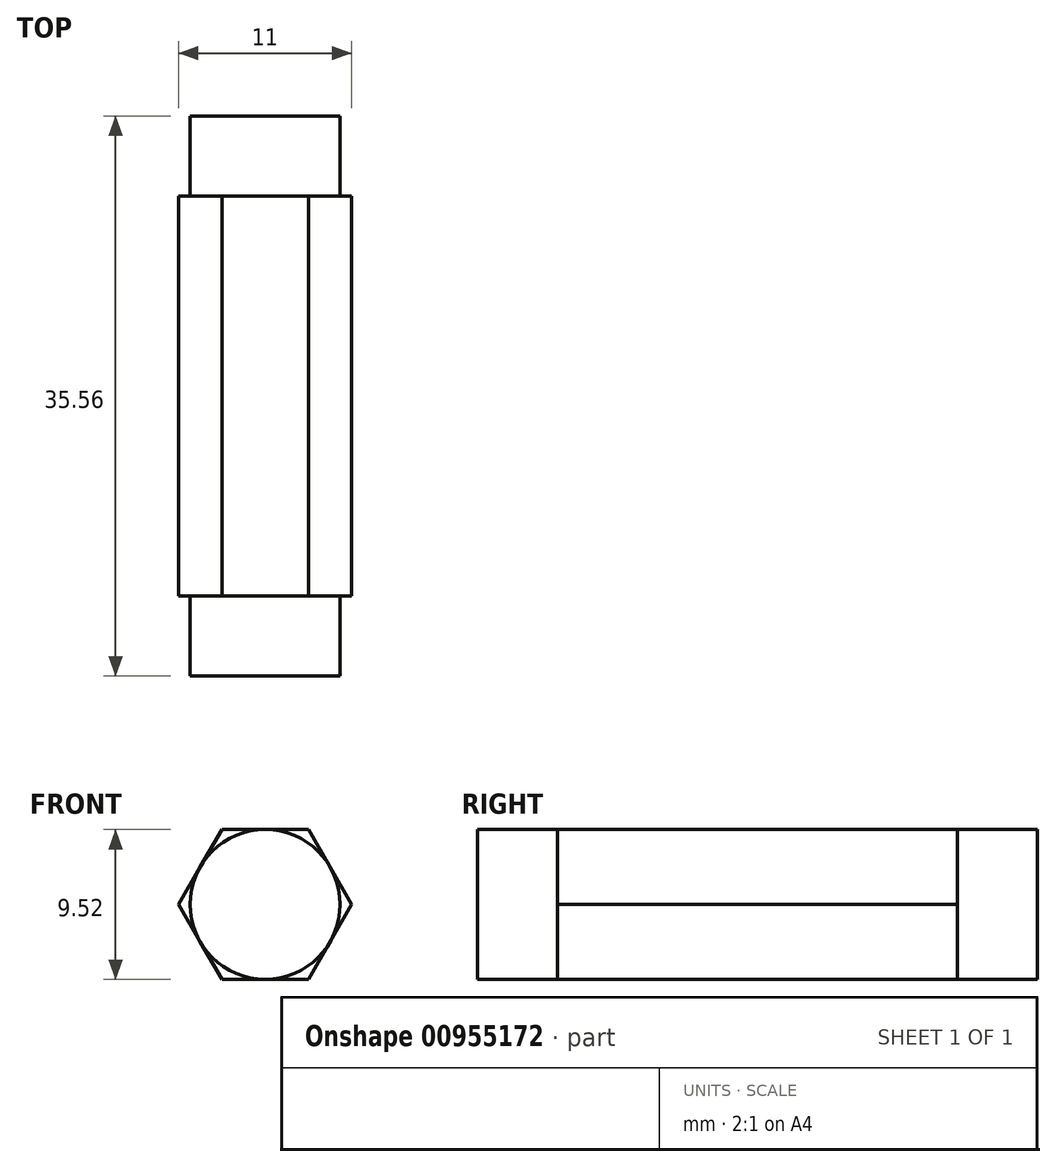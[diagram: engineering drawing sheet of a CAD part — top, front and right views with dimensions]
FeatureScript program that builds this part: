
annotation { "Feature Type Name" : "Feature", "Feature Type Description" : "" }
export const myFeature = defineFeature(function(context is Context, id is Id, definition is map)
    precondition{}
    {
        {
            var Q0;
            Q0=qCreatedBy(makeId("Front.planeOp"),FACE);
            var sketch = newSketch(context, id + "F0", { "sketchPlane" : qUnion([Q0])});
            skCircle(sketch, "E0.cCircle", {"center": v(0, 0) * mm, "radius": 4.76 * mm, "construction": true});
            skLineSegment(sketch, "E0.0", {"start": v(-2.75, 4.76) * mm, "end": v(2.75, 4.76) * mm});
            skLineSegment(sketch, "E0.1", {"start": v(2.75, 4.76) * mm, "end": v(5.5, 0) * mm});
            skLineSegment(sketch, "E0.2", {"start": v(5.5, 0) * mm, "end": v(2.75, -4.76) * mm});
            skLineSegment(sketch, "E0.3", {"start": v(2.75, -4.76) * mm, "end": v(-2.75, -4.76) * mm});
            skLineSegment(sketch, "E0.4", {"start": v(-2.75, -4.76) * mm, "end": v(-5.5, 0) * mm});
            skLineSegment(sketch, "E0.5", {"start": v(-5.5, 0) * mm, "end": v(-2.75, 4.76) * mm});
            skPoint(sketch, "E0.0.midPoint", {"position": v(0, 4.76) * mm});
            skSolve(sketch);
        }
        {
            var Q0;
            Q0=qSketchRegion(id+"F0",true);
            extrude(context, id + "F1", {"entities" : qUnion([Q0]), "depth" : 25.4 * mm, "offsetDistance" : 25.4 * mm});
        }
        {
            var Q0;
            Q0=makeQuery(id+"F1.opExtrude","CAP_FACE",FACE,{"disambiguationData":[OSD([sQuery(id+"F0.wireOp",EDGE,"E0.0"),sQuery(id+"F0.wireOp",EDGE,"E0.1"),sQuery(id+"F0.wireOp",EDGE,"E0.2"),sQuery(id+"F0.wireOp",EDGE,"E0.3"),sQuery(id+"F0.wireOp",EDGE,"E0.4"),sQuery(id+"F0.wireOp",EDGE,"E0.5")])],"isStart":false});
            var sketch = newSketch(context, id + "F2", { "sketchPlane" : qUnion([Q0])});
            skCircle(sketch, "E1", {"center": v(0, 0) * mm, "radius": 4.76 * mm});
            skSolve(sketch);
        }
        {
            var Q0;
            Q0=qSketchRegion(id+"F2",true);
            extrude(context, id + "F3", {"entities" : qUnion([Q0]), "operationType" : NewBodyOperationType.ADD, "depth" : 5.08 * mm, "offsetDistance" : 25.4 * mm});
        }
        {
            var Q0;
            Q0=makeQuery(id+"F1.opExtrude","CAP_FACE",FACE,{"disambiguationData":[OSD([sQuery(id+"F0.wireOp",EDGE,"E0.0"),sQuery(id+"F0.wireOp",EDGE,"E0.1"),sQuery(id+"F0.wireOp",EDGE,"E0.2"),sQuery(id+"F0.wireOp",EDGE,"E0.3"),sQuery(id+"F0.wireOp",EDGE,"E0.4"),sQuery(id+"F0.wireOp",EDGE,"E0.5")])],"isStart":true});
            var sketch = newSketch(context, id + "F4", { "sketchPlane" : qUnion([Q0])});
            skCircle(sketch, "E2", {"center": v(0, 0) * mm, "radius": 4.76 * mm});
            skSolve(sketch);
        }
        {
            var Q0;
            Q0=qSketchRegion(id+"F4",true);
            extrude(context, id + "F5", {"entities" : qUnion([Q0]), "operationType" : NewBodyOperationType.ADD, "depth" : 5.08 * mm, "offsetDistance" : 25.4 * mm});
        }
    });
